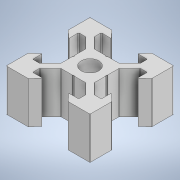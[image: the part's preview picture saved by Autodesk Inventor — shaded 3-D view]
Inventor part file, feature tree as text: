
AUTODESK INVENTOR PART (.ipt)
format: ipt  version: 2021 (Build 250183000, 183)  size: 232,960 bytes
history: native  units: mm
features: sketch x3, extrude x2, fillet x2, other x1, pattern_circular x1, hole x1, projected_geometry x1
ambient origin geometry x8: Origin, YZ Plane, XZ Plane, XY Plane, X Axis, Y Axis, Z Axis, Center Point
bodies: Body1 (feature_tree)
feature tree (11):
  other  "實體1"
  extrude  "擠出1"  Depth=20.0mm
  extrude  "擠出2"  Depth=20.0mm
  fillet  "圓角1"  Radius=10.0mm
  pattern_circular  "環形陣列1"  [2 undecoded]
  hole  "孔1"  [1 undecoded]
  fillet  "圓角2"  Radius=6.2mm
  sketch  "草圖1"
  sketch  "草圖2"
  projected_geometry  "投影迴路1"
  sketch  "草圖3"
note: 3 required parameter values undecoded (feature->parameter linkage not recoverable at this tier; creation-order binding heuristic only, values carry confidence <= 0.55)
